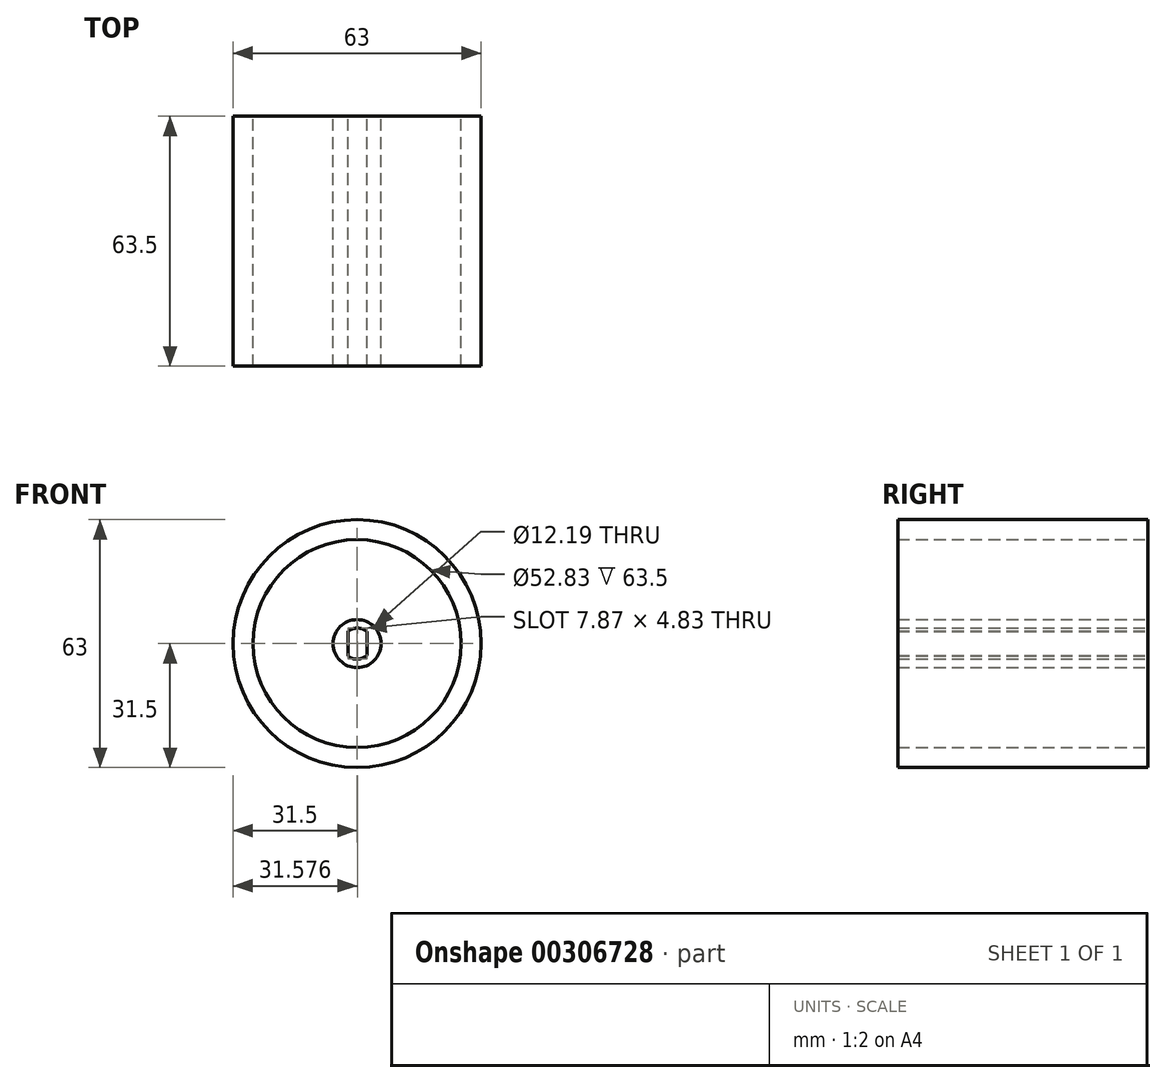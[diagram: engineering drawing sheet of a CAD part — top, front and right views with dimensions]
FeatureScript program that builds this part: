
annotation { "Feature Type Name" : "Feature", "Feature Type Description" : "" }
export const myFeature = defineFeature(function(context is Context, id is Id, definition is map)
    precondition{}
    {
        {
            var Q0;
            Q0=qCreatedBy(makeId("Front.planeOp"),FACE);
            var sketch = newSketch(context, id + "F0", { "sketchPlane" : qUnion([Q0])});
            skCircle(sketch, "E0", {"center": v(0, 0) * mm, "radius": 31.5 * mm});
            skCircle(sketch, "E1", {"center": v(0, 0) * mm, "radius": 6.1 * mm});
            skCircle(sketch, "E2", {"center": v(0, 0) * mm, "radius": 3.94 * mm});
            skLineSegment(sketch, "E3", {"start": v(-2.34, 3.17) * mm, "end": v(-2.34, -3.17) * mm});
            skLineSegment(sketch, "E4", {"start": v(2.49, 3.05) * mm, "end": v(2.49, -3.05) * mm});
            skCircle(sketch, "E5", {"center": v(0, 0) * mm, "radius": 26.42 * mm});
            skLineSegment(sketch, "E6", {"start": v(-6.1, 0.2) * mm, "end": v(-6.1, 25.7) * mm});
            skLineSegment(sketch, "E7", {"start": v(-3.55, 26.18) * mm, "end": v(-3.55, 4.95) * mm});
            skLineSegment(sketch, "E8", {"start": v(2.88, -5.37) * mm, "end": v(-19.21, -18.13) * mm});
            skLineSegment(sketch, "E9", {"start": v(3.22, 5.18) * mm, "end": v(25.3, -7.58) * mm});
            skLineSegment(sketch, "E10", {"start": v(-3.2, 5.2) * mm, "end": v(-25.34, -7.47) * mm});
            skLineSegment(sketch, "E11", {"start": v(-2.88, -5.37) * mm, "end": v(19.21, -18.13) * mm});
            skSolve(sketch);
        }
        {
            var Q0;
            Q0 = qSketchRegion(id + "F0", true);
            extrude(context, id + "F1", {"entities" : qUnion([Q0]), "depth" : 63.5 * mm});
        }
        {
            var Q0;
            Q0=makeQuery(id+"F0.imprint","IMPRINT",FACE,{"disambiguationData":[TD([[makeQuery(id+"F0.imprint","IMPRINT",EDGE,{"derivedFrom":sQuery(id+"F0.wireOp",EDGE,"E1")}),1.0]])]});
            var Q1;
            {var subQ0=sQuery(id+"F0.wireOp",EDGE,"E3");Q1=makeQuery(id+"F0.imprint","IMPRINT",FACE,{"disambiguationData":[TD([[makeQuery(id+"F0.imprint","IMPRINT",EDGE,{"derivedFrom":subQ0}),-1.0]])]});}
            var Q2;
            {var subQ0=sQuery(id+"F0.wireOp",EDGE,"E4");Q2=makeQuery(id+"F0.imprint","IMPRINT",FACE,{"disambiguationData":[TD([[makeQuery(id+"F0.imprint","IMPRINT",EDGE,{"derivedFrom":subQ0}),1.0]])]});}
            extrude(context, id + "F2", {"entities" : qUnion([Q0, Q1, Q2]), "operationType" : NewBodyOperationType.ADD, "depth" : 63.5 * mm});
        }
        {
            var Q0;
            {var subQ0=sQuery(id+"F0.wireOp",EDGE,"E8");Q0=makeQuery(id+"F0.imprint","IMPRINT",FACE,{"disambiguationData":[TD([[makeQuery(id+"F0.imprint","IMPRINT",EDGE,{"derivedFrom":subQ0}),-1.0]])]});}
            var Q1;
            {var subQ0=sQuery(id+"F0.wireOp",EDGE,"E9");Q1=makeQuery(id+"F0.imprint","IMPRINT",FACE,{"disambiguationData":[TD([[makeQuery(id+"F0.imprint","IMPRINT",EDGE,{"derivedFrom":subQ0}),-1.0]])]});}
            var Q2;
            {var subQ0=sQuery(id+"F0.wireOp",EDGE,"E6");Q2=makeQuery(id+"F0.imprint","IMPRINT",FACE,{"disambiguationData":[TD([[makeQuery(id+"F0.imprint","IMPRINT",EDGE,{"derivedFrom":subQ0}),-1.0]])]});}
            var Q3;
            {var subQ0=sQuery(id+"F0.wireOp",EDGE,"E6");Q3=makeQuery(id+"F0.imprint","IMPRINT",FACE,{"disambiguationData":[TD([[makeQuery(id+"F0.imprint","IMPRINT",EDGE,{"derivedFrom":subQ0}),1.0]])]});}
            var Q4;
            {var subQ0=sQuery(id+"F0.wireOp",EDGE,"E7");Q4=makeQuery(id+"F0.imprint","IMPRINT",FACE,{"disambiguationData":[TD([[makeQuery(id+"F0.imprint","IMPRINT",EDGE,{"derivedFrom":subQ0}),1.0]])]});}
            var Q5;
            {var subQ0=sQuery(id+"F0.wireOp",EDGE,"E8");Q5=makeQuery(id+"F0.imprint","IMPRINT",FACE,{"disambiguationData":[TD([[makeQuery(id+"F0.imprint","IMPRINT",EDGE,{"derivedFrom":subQ0}),1.0]])]});}
            var Q6;
            {var subQ5=sQuery(id+"F0.wireOp",EDGE,"E6");var subQ6=sQuery(id+"F0.wireOp",EDGE,"E1");var subQ7=makeQuery(id+"F0.imprint","INTERSECT",VERTEX,{"derivedFrom":[subQ6,subQ5]});Q6=makeQuery(id+"F0.imprint","IMPRINT",FACE,{"disambiguationData":[TD([[makeQuery(id+"F0.imprint","IMPRINT",EDGE,{"disambiguationData":[TD([[subQ7,-1.0]])],"derivedFrom":subQ6}),-1.0]])]});}
            var Q7;
            {var subQ0=sQuery(id+"F0.wireOp",EDGE,"E9");Q7=makeQuery(id+"F0.imprint","IMPRINT",FACE,{"disambiguationData":[TD([[makeQuery(id+"F0.imprint","IMPRINT",EDGE,{"derivedFrom":subQ0}),1.0]])]});}
            extrude(context, id + "F3", {"entities" : qUnion([Q0, Q1, Q2, Q3, Q4, Q5, Q6, Q7]), "depth" : 63.5 * mm});
        }
    });
